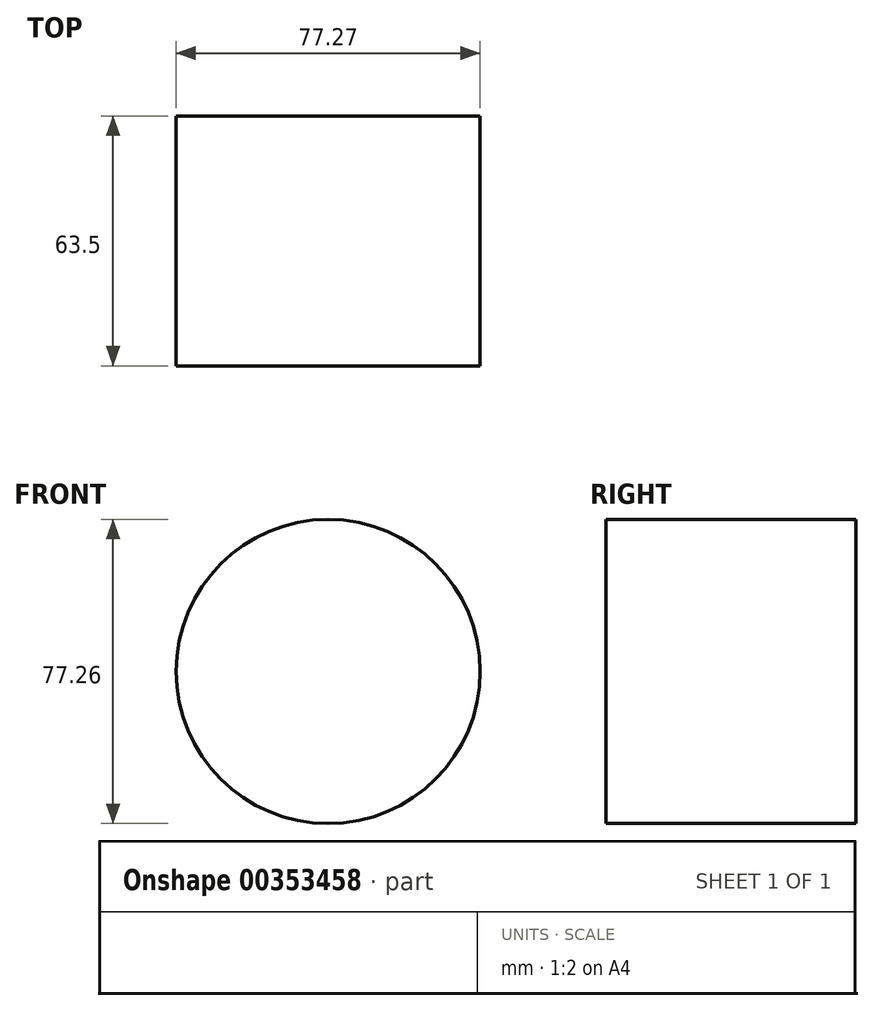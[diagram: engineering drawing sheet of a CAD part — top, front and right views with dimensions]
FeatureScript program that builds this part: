
annotation { "Feature Type Name" : "Feature", "Feature Type Description" : "" }
export const myFeature = defineFeature(function(context is Context, id is Id, definition is map)
    precondition{}
    {
        {
            var Q0;
            Q0=qCreatedBy(makeId("Front.planeOp"),FACE);
            var sketch = newSketch(context, id + "F0", { "sketchPlane" : qUnion([Q0])});
            skCircle(sketch, "E0", {"center": v(-44.88, 52.46) * mm, "radius": 38.63 * mm});
            skSolve(sketch);
        }
        {
            var Q0;
            Q0 = qSketchRegion(id + "F0", true);
            extrude(context, id + "F1", {"entities" : qUnion([Q0]), "depth" : 63.5 * mm});
        }
    });
